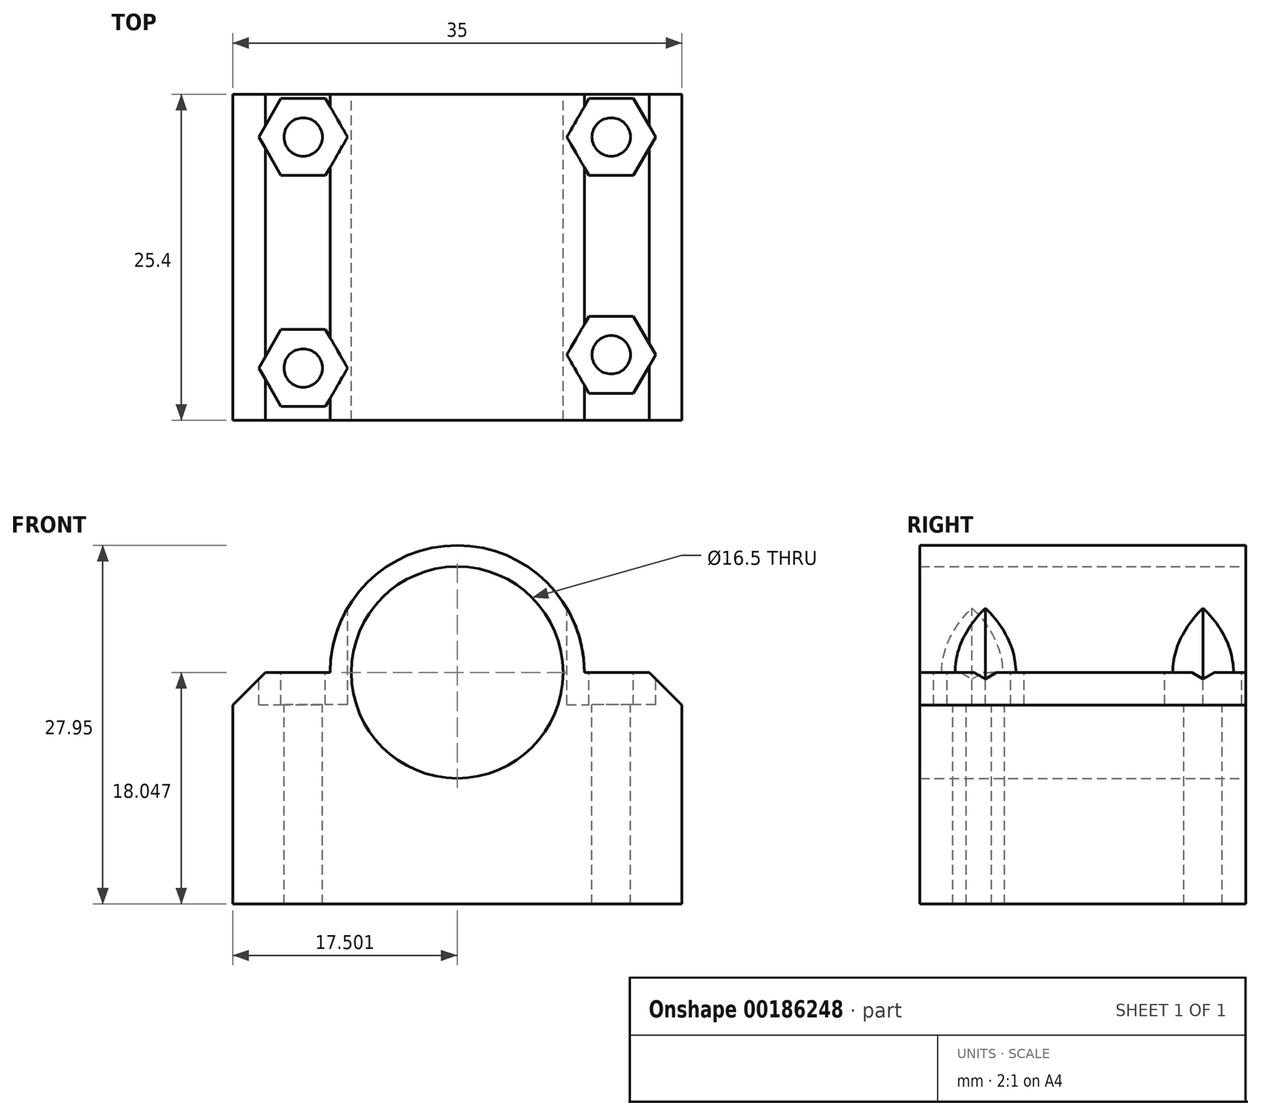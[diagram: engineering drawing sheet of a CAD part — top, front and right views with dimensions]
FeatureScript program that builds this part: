
annotation { "Feature Type Name" : "Feature", "Feature Type Description" : "" }
export const myFeature = defineFeature(function(context is Context, id is Id, definition is map)
    precondition{}
    {
        {
            var Q0;
            Q0=qCreatedBy(makeId("Front.planeOp"),FACE);
            var sketch = newSketch(context, id + "F0", { "sketchPlane" : qUnion([Q0])});
            skArc(sketch, "E0", {"start": v(-21.02, 14.44) * mm, "mid": v(-30.93, 24.34) * mm, "end": v(-40.84, 14.44) * mm});
            skLineSegment(sketch, "E1.bottom", {"start": v(-48.43, 14.44) * mm, "end": v(-40.84, 14.44) * mm});
            skLineSegment(sketch, "E1.top", {"start": v(-48.43, -3.61) * mm, "end": v(-13.43, -3.61) * mm});
            skLineSegment(sketch, "E1.left", {"start": v(-48.43, 14.44) * mm, "end": v(-48.43, -3.61) * mm});
            skLineSegment(sketch, "E1.right", {"start": v(-13.43, 14.44) * mm, "end": v(-13.43, -3.61) * mm});
            skLineSegment(sketch, "E2.trimOffspring", {"start": v(-21.02, 14.44) * mm, "end": v(-13.43, 14.44) * mm});
            skPoint(sketch, "E3", {"position": v(-30.93, 4.39) * mm});
            skCircle(sketch, "E4", {"center": v(-30.93, 14.44) * mm, "radius": 8.25 * mm});
            skSolve(sketch);
        }
        {
            var Q0;
            Q0 = qSketchRegion(id + "F0", true);
            extrude(context, id + "F1", {"entities" : qUnion([Q0]), "depth" : 25.4 * mm});
        }
        {
            var Q0;
            Q0=makeQuery(id+"F1.opExtrude","SWEPT_FACE",FACE,{"disambiguationData":[OSD([sQuery(id+"F0.wireOp",EDGE,"E1.bottom")])]});
            var sketch = newSketch(context, id + "F2", { "sketchPlane" : qUnion([Q0])});
            skCircle(sketch, "E5", {"center": v(-42.93, -21.33) * mm, "radius": 1.5 * mm});
            skPoint(sketch, "E5.centerSnap0", {"position": v(-44.63, 0) * mm});
            skCircle(sketch, "E6", {"center": v(-42.93, -3.33) * mm, "radius": 1.5 * mm});
            skCircle(sketch, "E7", {"center": v(-18.93, -3.33) * mm, "radius": 1.5 * mm});
            skCircle(sketch, "E8", {"center": v(-18.93, -20.3) * mm, "radius": 1.5 * mm});
            skLineSegment(sketch, "E9", {"start": v(-42.93, -3.33) * mm, "end": v(-48.43, -3.33) * mm, "construction": true});
            skLineSegment(sketch, "E10", {"start": v(-18.93, -3.33) * mm, "end": v(-13.43, -3.33) * mm, "construction": true});
            skSolve(sketch);
        }
        {
            var Q0;
            Q0 = qSketchRegion(id + "F2", true);
            extrude(context, id + "F3", {"entities" : qUnion([Q0]), "operationType" : NewBodyOperationType.REMOVE, "endBound" : BoundingType.THROUGH_ALL, "oppositeDirection" : true, "depth" : 25.4 * mm});
        }
        {
            var Q0;
            Q0=makeQuery(id+"F1.opExtrude","SWEPT_EDGE",EDGE,{"disambiguationData":[OSD([sQuery(id+"F0.wireOp",EDGE,"E1.bottom"),sQuery(id+"F0.wireOp",EDGE,"E1.left")])]});
            var Q1;
            Q1=makeQuery(id+"F1.opExtrude","SWEPT_EDGE",EDGE,{"disambiguationData":[OSD([sQuery(id+"F0.wireOp",EDGE,"E1.right"),sQuery(id+"F0.wireOp",EDGE,"E2.trimOffspring")])]});
            chamfer(context, id + "F4", {"entities" : qUnion([Q0, Q1]), "width" : 2.54 * mm, "tangentPropagation" : true});
        }
        {
            var Q0;
            Q0=makeQuery(id+"F1.opExtrude","SWEPT_FACE",FACE,{"disambiguationData":[OSD([sQuery(id+"F0.wireOp",EDGE,"E1.bottom")])]});
            var sketch = newSketch(context, id + "F5", { "sketchPlane" : qUnion([Q0])});
            skCircle(sketch, "E11.0", {"center": v(-42.93, -3.33) * mm, "radius": 1.5 * mm});
            skCircle(sketch, "E12.0", {"center": v(-42.93, -21.33) * mm, "radius": 1.5 * mm});
            skCircle(sketch, "E13.0", {"center": v(-18.93, -20.3) * mm, "radius": 1.5 * mm});
            skCircle(sketch, "E14.0", {"center": v(-18.93, -3.33) * mm, "radius": 1.5 * mm});
            skCircle(sketch, "E15.cCircle", {"center": v(-42.93, -3.33) * mm, "radius": 3 * mm, "construction": true});
            skLineSegment(sketch, "E15.0", {"start": v(-41.2, -6.33) * mm, "end": v(-44.66, -6.33) * mm});
            skLineSegment(sketch, "E15.1", {"start": v(-44.66, -6.33) * mm, "end": v(-46.4, -3.33) * mm});
            skLineSegment(sketch, "E15.2", {"start": v(-46.4, -3.33) * mm, "end": v(-44.66, -0.33) * mm});
            skLineSegment(sketch, "E15.3", {"start": v(-44.66, -0.33) * mm, "end": v(-41.2, -0.33) * mm});
            skLineSegment(sketch, "E15.4", {"start": v(-41.2, -0.33) * mm, "end": v(-39.46, -3.33) * mm});
            skLineSegment(sketch, "E15.5", {"start": v(-39.46, -3.33) * mm, "end": v(-41.2, -6.33) * mm});
            skPoint(sketch, "E15.0.midPoint", {"position": v(-42.93, -6.33) * mm});
            skCircle(sketch, "E16.cCircle", {"center": v(-42.93, -21.33) * mm, "radius": 3 * mm, "construction": true});
            skLineSegment(sketch, "E16.0", {"start": v(-41.2, -24.33) * mm, "end": v(-44.66, -24.33) * mm});
            skLineSegment(sketch, "E16.1", {"start": v(-44.66, -24.33) * mm, "end": v(-46.4, -21.33) * mm});
            skLineSegment(sketch, "E16.2", {"start": v(-46.4, -21.33) * mm, "end": v(-44.66, -18.33) * mm});
            skLineSegment(sketch, "E16.3", {"start": v(-44.66, -18.33) * mm, "end": v(-41.2, -18.33) * mm});
            skLineSegment(sketch, "E16.4", {"start": v(-41.2, -18.33) * mm, "end": v(-39.46, -21.33) * mm});
            skLineSegment(sketch, "E16.5", {"start": v(-39.46, -21.33) * mm, "end": v(-41.2, -24.33) * mm});
            skPoint(sketch, "E16.0.midPoint", {"position": v(-42.93, -24.33) * mm});
            skCircle(sketch, "E17.cCircle", {"center": v(-18.93, -3.33) * mm, "radius": 3 * mm, "construction": true});
            skLineSegment(sketch, "E17.0", {"start": v(-17.2, -6.33) * mm, "end": v(-20.66, -6.33) * mm});
            skLineSegment(sketch, "E17.1", {"start": v(-20.66, -6.33) * mm, "end": v(-22.4, -3.33) * mm});
            skLineSegment(sketch, "E17.2", {"start": v(-22.4, -3.33) * mm, "end": v(-20.66, -0.33) * mm});
            skLineSegment(sketch, "E17.3", {"start": v(-20.66, -0.33) * mm, "end": v(-17.2, -0.33) * mm});
            skLineSegment(sketch, "E17.4", {"start": v(-17.2, -0.33) * mm, "end": v(-15.46, -3.33) * mm});
            skLineSegment(sketch, "E17.5", {"start": v(-15.46, -3.33) * mm, "end": v(-17.2, -6.33) * mm});
            skPoint(sketch, "E17.0.midPoint", {"position": v(-18.93, -6.33) * mm});
            skCircle(sketch, "E18.cCircle", {"center": v(-18.93, -20.3) * mm, "radius": 3 * mm, "construction": true});
            skLineSegment(sketch, "E18.0", {"start": v(-17.2, -23.3) * mm, "end": v(-20.66, -23.3) * mm});
            skLineSegment(sketch, "E18.1", {"start": v(-20.66, -23.3) * mm, "end": v(-22.4, -20.3) * mm});
            skLineSegment(sketch, "E18.2", {"start": v(-22.4, -20.3) * mm, "end": v(-20.66, -17.3) * mm});
            skLineSegment(sketch, "E18.3", {"start": v(-20.66, -17.3) * mm, "end": v(-17.2, -17.3) * mm});
            skLineSegment(sketch, "E18.4", {"start": v(-17.2, -17.3) * mm, "end": v(-15.46, -20.3) * mm});
            skLineSegment(sketch, "E18.5", {"start": v(-15.46, -20.3) * mm, "end": v(-17.2, -23.3) * mm});
            skPoint(sketch, "E18.0.midPoint", {"position": v(-18.93, -23.3) * mm});
            skSolve(sketch);
        }
        {
            var Q0;
            Q0 = qSketchRegion(id + "F5", true);
            extrude(context, id + "F6", {"entities" : qUnion([Q0]), "operationType" : NewBodyOperationType.REMOVE, "oppositeDirection" : true, "depth" : 2.5 * mm, "hasSecondDirection" : true, "secondDirectionOppositeDirection" : false, "secondDirectionDepth" : 25.4 * mm});
        }
    });
